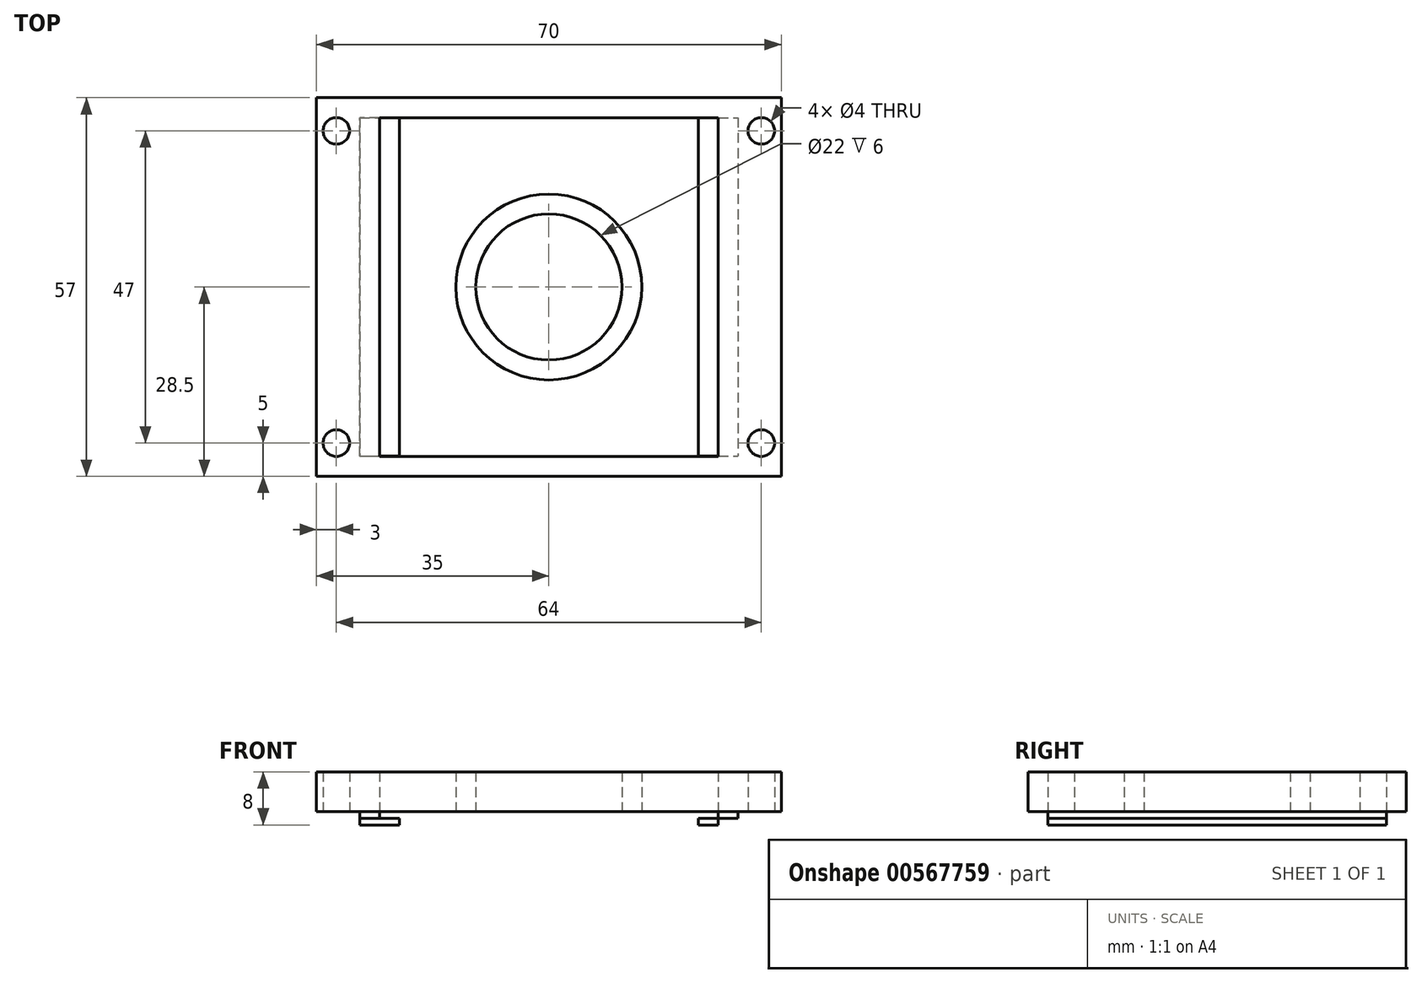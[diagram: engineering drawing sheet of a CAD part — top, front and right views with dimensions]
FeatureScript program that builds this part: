
annotation { "Feature Type Name" : "Feature", "Feature Type Description" : "" }
export const myFeature = defineFeature(function(context is Context, id is Id, definition is map)
    precondition{}
    {
        {
            var Q0;
            Q0=qCreatedBy(makeId("Top.planeOp"),FACE);
            var sketch = newSketch(context, id + "F0", { "sketchPlane" : qUnion([Q0])});
            skCircle(sketch, "E0", {"center": v(0, 0) * mm, "radius": 11 * mm});
            skCircle(sketch, "E1", {"center": v(0, 0) * mm, "radius": 14 * mm});
            skSolve(sketch);
        }
        {
            var Q0;
            Q0=makeQuery(id+"F0.imprint","IMPRINT",FACE,{"disambiguationData":[TD([[makeQuery(id+"F0.imprint","IMPRINT",EDGE,{"derivedFrom":sQuery(id+"F0.wireOp",EDGE,"E0")}),-1.0]])]});
            extrude(context, id + "F1", {"entities" : qUnion([Q0]), "depth" : 6 * mm, "offsetDistance" : 25 * mm});
        }
        {
            var Q0;
            Q0=makeQuery(id+"F1.opExtrude","CAP_FACE",FACE,{"disambiguationData":[OSD([sQuery(id+"F0.wireOp",EDGE,"E0"),sQuery(id+"F0.wireOp",EDGE,"E1")])],"isStart":true});
            var sketch = newSketch(context, id + "F2", { "sketchPlane" : qUnion([Q0])});
            skLineSegment(sketch, "E2.bottom", {"start": v(25.5, -25.5) * mm, "end": v(-25.5, -25.5) * mm});
            skLineSegment(sketch, "E2.top", {"start": v(25.5, 25.5) * mm, "end": v(-25.5, 25.5) * mm});
            skLineSegment(sketch, "E2.left", {"start": v(25.5, -25.5) * mm, "end": v(25.5, 25.5) * mm});
            skLineSegment(sketch, "E2.right", {"start": v(-25.5, -25.5) * mm, "end": v(-25.5, 25.5) * mm});
            skPoint(sketch, "E2.middle", {"position": v(0, 0) * mm});
            skLineSegment(sketch, "E3.bottom", {"start": v(28.5, 28.5) * mm, "end": v(-28.5, 28.5) * mm});
            skLineSegment(sketch, "E3.top", {"start": v(28.5, -28.5) * mm, "end": v(-28.5, -28.5) * mm});
            skLineSegment(sketch, "E3.left", {"start": v(28.5, 28.5) * mm, "end": v(28.5, -28.5) * mm});
            skLineSegment(sketch, "E3.right", {"start": v(-28.5, 28.5) * mm, "end": v(-28.5, -28.5) * mm});
            skLineSegment(sketch, "E4.bottom", {"start": v(-25.5, -2.53) * mm, "end": v(-13.7, -2.53) * mm});
            skLineSegment(sketch, "E4.top", {"start": v(-25.5, 2.53) * mm, "end": v(-13.7, 2.53) * mm});
            skLineSegment(sketch, "E4.left", {"start": v(-25.5, -2.53) * mm, "end": v(-25.5, 2.53) * mm});
            skLineSegment(sketch, "E4.right", {"start": v(25.5, -2.53) * mm, "end": v(25.5, 2.53) * mm});
            skLineSegment(sketch, "E5.bottom", {"start": v(-2.33, 25.5) * mm, "end": v(2.33, 25.5) * mm});
            skLineSegment(sketch, "E5.top", {"start": v(-2.33, -25.5) * mm, "end": v(2.33, -25.5) * mm});
            skLineSegment(sketch, "E5.left", {"start": v(-2.33, 25.5) * mm, "end": v(-2.33, 13.74) * mm});
            skLineSegment(sketch, "E5.right", {"start": v(2.33, 25.5) * mm, "end": v(2.33, 13.74) * mm});
            skArc(sketch, "E6", {"start": v(2.33, 13.74) * mm, "mid": v(0, 13.94) * mm, "end": v(-2.33, 13.74) * mm});
            skLineSegment(sketch, "E7.trimOffspring", {"start": v(13.7, -2.53) * mm, "end": v(25.5, -2.53) * mm});
            skLineSegment(sketch, "E8.trimOffspring", {"start": v(13.7, 2.53) * mm, "end": v(25.5, 2.53) * mm});
            skLineSegment(sketch, "E9.trimOffspring", {"start": v(2.33, -13.74) * mm, "end": v(2.33, -25.5) * mm});
            skLineSegment(sketch, "E10.trimOffspring", {"start": v(-2.33, -13.74) * mm, "end": v(-2.33, -25.5) * mm});
            skArc(sketch, "E11.trimOffspring", {"start": v(-2.33, -13.74) * mm, "mid": v(0, -13.94) * mm, "end": v(2.33, -13.74) * mm});
            skArc(sketch, "E12.trimOffspring", {"start": v(13.7, -2.53) * mm, "mid": v(13.94, 0) * mm, "end": v(13.7, 2.53) * mm});
            skArc(sketch, "E13.trimOffspring", {"start": v(-13.7, 2.53) * mm, "mid": v(-13.94, 0) * mm, "end": v(-13.7, -2.53) * mm});
            skSolve(sketch);
        }
        {
            var Q0;
            Q0 = qSketchRegion(id + "F2", true);
            var Q1;
            {var subQ0=sQuery(id+"F2.wireOp",EDGE,"E5.bottom");Q1=makeQuery(id+"F2.imprint","IMPRINT",FACE,{"disambiguationData":[TD([[makeQuery(id+"F2.imprint","IMPRINT",EDGE,{"derivedFrom":subQ0}),-1.0]])]});}
            var Q2;
            {var subQ0=sQuery(id+"F2.wireOp",EDGE,"E4.left");Q2=makeQuery(id+"F2.imprint","IMPRINT",FACE,{"disambiguationData":[TD([[makeQuery(id+"F2.imprint","IMPRINT",EDGE,{"derivedFrom":subQ0}),-1.0]])]});}
            var Q3;
            {var subQ0=sQuery(id+"F2.wireOp",EDGE,"E5.top");Q3=makeQuery(id+"F2.imprint","IMPRINT",FACE,{"disambiguationData":[TD([[makeQuery(id+"F2.imprint","IMPRINT",EDGE,{"derivedFrom":subQ0}),1.0]])]});}
            var Q4;
            {var subQ0=sQuery(id+"F2.wireOp",EDGE,"E4.right");Q4=makeQuery(id+"F2.imprint","IMPRINT",FACE,{"disambiguationData":[TD([[makeQuery(id+"F2.imprint","IMPRINT",EDGE,{"derivedFrom":subQ0}),1.0]])]});}
            extrude(context, id + "F3", {"entities" : qUnion([Q0, Q1, Q2, Q3, Q4]), "oppositeDirection" : true, "depth" : 6 * mm, "offsetDistance" : 25 * mm});
        }
        {
            var Q0;
            Q0=makeQuery(id+"F1.opExtrude","SWEPT_BODY",BODY,{"disambiguationData":[OSD([sQuery(id+"F0.wireOp",EDGE,"E0"),sQuery(id+"F0.wireOp",EDGE,"E1")])]});
            var Q1;
            Q1=makeQuery(id+"F3.opExtrude","SWEPT_BODY",BODY,{"disambiguationData":[OSD([sQuery(id+"F0.wireOp",EDGE,"E1"),sQuery(id+"F2.wireOp",EDGE,"E2.bottom"),sQuery(id+"F2.wireOp",EDGE,"E2.top"),sQuery(id+"F2.wireOp",EDGE,"E2.left"),sQuery(id+"F2.wireOp",EDGE,"E2.right"),sQuery(id+"F2.wireOp",EDGE,"E3.bottom"),sQuery(id+"F2.wireOp",EDGE,"E3.top"),sQuery(id+"F2.wireOp",EDGE,"E3.left"),sQuery(id+"F2.wireOp",EDGE,"E3.right"),sQuery(id+"F2.wireOp",EDGE,"E4.bottom"),sQuery(id+"F2.wireOp",EDGE,"E4.top"),sQuery(id+"F2.wireOp",EDGE,"E5.left"),sQuery(id+"F2.wireOp",EDGE,"E5.right"),sQuery(id+"F2.wireOp",EDGE,"E7.trimOffspring"),sQuery(id+"F2.wireOp",EDGE,"E8.trimOffspring"),sQuery(id+"F2.wireOp",EDGE,"E9.trimOffspring"),sQuery(id+"F2.wireOp",EDGE,"E10.trimOffspring")])]});
            booleanBodies(context, id + "F4", {"operationType" : BooleanOperationType.UNION, "tools" : qUnion([Q0, Q1])});
        }
        {
            var Q0;
            {var subQ0=sQuery(id+"F0.wireOp",EDGE,"E1");Q0=makeQuery(id+"F4.opBoolean","MERGE",FACE,{"derivedFrom":[makeQuery(id+"F1.opExtrude","CAP_FACE",FACE,{"disambiguationData":[OSD([sQuery(id+"F0.wireOp",EDGE,"E0"),subQ0])],"isStart":true}),makeQuery(id+"F3.opExtrude","CAP_FACE",FACE,{"disambiguationData":[OSD([subQ0,sQuery(id+"F2.wireOp",EDGE,"E2.bottom"),sQuery(id+"F2.wireOp",EDGE,"E2.top"),sQuery(id+"F2.wireOp",EDGE,"E2.left"),sQuery(id+"F2.wireOp",EDGE,"E2.right"),sQuery(id+"F2.wireOp",EDGE,"E3.bottom"),sQuery(id+"F2.wireOp",EDGE,"E3.top"),sQuery(id+"F2.wireOp",EDGE,"E3.left"),sQuery(id+"F2.wireOp",EDGE,"E3.right"),sQuery(id+"F2.wireOp",EDGE,"E4.bottom"),sQuery(id+"F2.wireOp",EDGE,"E4.top"),sQuery(id+"F2.wireOp",EDGE,"E5.left"),sQuery(id+"F2.wireOp",EDGE,"E5.right"),sQuery(id+"F2.wireOp",EDGE,"E7.trimOffspring"),sQuery(id+"F2.wireOp",EDGE,"E8.trimOffspring"),sQuery(id+"F2.wireOp",EDGE,"E9.trimOffspring"),sQuery(id+"F2.wireOp",EDGE,"E10.trimOffspring")])],"isStart":true})]});}
            var sketch = newSketch(context, id + "F5", { "sketchPlane" : qUnion([Q0])});
            skLineSegment(sketch, "E14.bottom", {"start": v(25.5, -25.5) * mm, "end": v(28.5, -25.5) * mm});
            skLineSegment(sketch, "E14.top", {"start": v(25.5, 25.48) * mm, "end": v(28.5, 25.48) * mm});
            skLineSegment(sketch, "E14.left", {"start": v(25.5, -25.5) * mm, "end": v(25.5, 25.48) * mm});
            skLineSegment(sketch, "E14.right", {"start": v(28.5, -25.5) * mm, "end": v(28.5, 25.48) * mm});
            skLineSegment(sketch, "E15.bottom", {"start": v(-25.5, -25.5) * mm, "end": v(-28.5, -25.5) * mm});
            skLineSegment(sketch, "E15.top", {"start": v(-25.5, 25.5) * mm, "end": v(-28.5, 25.5) * mm});
            skLineSegment(sketch, "E15.left", {"start": v(-25.5, -25.5) * mm, "end": v(-25.5, 25.5) * mm});
            skLineSegment(sketch, "E15.right", {"start": v(-28.5, -25.5) * mm, "end": v(-28.5, 25.5) * mm});
            skSolve(sketch);
        }
        {
            var Q0;
            Q0 = qSketchRegion(id + "F5", true);
            extrude(context, id + "F6", {"entities" : qUnion([Q0]), "operationType" : NewBodyOperationType.ADD, "depth" : 1 * mm, "offsetDistance" : 25 * mm});
        }
        {
            var Q0;
            Q0=makeQuery(id+"F6.opExtrude","CAP_FACE",FACE,{"disambiguationData":[OSD([sQuery(id+"F5.wireOp",EDGE,"E14.bottom"),sQuery(id+"F5.wireOp",EDGE,"E14.top"),sQuery(id+"F5.wireOp",EDGE,"E14.left"),sQuery(id+"F5.wireOp",EDGE,"E14.right")])],"isStart":false});
            var sketch = newSketch(context, id + "F7", { "sketchPlane" : qUnion([Q0])});
            skLineSegment(sketch, "E16.bottom", {"start": v(28.5, -25.5) * mm, "end": v(22.5, -25.5) * mm});
            skLineSegment(sketch, "E16.top", {"start": v(28.5, 25.48) * mm, "end": v(22.5, 25.48) * mm});
            skLineSegment(sketch, "E16.left", {"start": v(28.5, -25.5) * mm, "end": v(28.5, 25.48) * mm});
            skLineSegment(sketch, "E16.right", {"start": v(22.5, -25.5) * mm, "end": v(22.5, 25.48) * mm});
            skLineSegment(sketch, "E17.bottom", {"start": v(-28.5, 25.48) * mm, "end": v(-22.5, 25.48) * mm});
            skLineSegment(sketch, "E17.top", {"start": v(-28.5, -25.49) * mm, "end": v(-22.5, -25.49) * mm});
            skLineSegment(sketch, "E17.left", {"start": v(-28.5, 25.48) * mm, "end": v(-28.5, -25.49) * mm});
            skLineSegment(sketch, "E17.right", {"start": v(-22.5, 25.48) * mm, "end": v(-22.5, -25.49) * mm});
            skSolve(sketch);
        }
        {
            var Q0;
            Q0=makeQuery(id+"F7.imprint","IMPRINT",FACE,{"disambiguationData":[TD([[makeQuery(id+"F7.imprint","IMPRINT",EDGE,{"derivedFrom":sQuery(id+"F7.wireOp",EDGE,"E17.bottom")}),-1.0]])]});
            var Q1;
            {var subQ2=sQuery(id+"F7.wireOp",EDGE,"E16.right");Q1=makeQuery(id+"F7.imprint","IMPRINT",FACE,{"disambiguationData":[TD([[makeQuery(id+"F7.imprint","IMPRINT",EDGE,{"derivedFrom":subQ2}),-1.0]])]});}
            var Q2;
            {var subQ2=sQuery(id+"F7.wireOp",EDGE,"E16.left");Q2=makeQuery(id+"F7.imprint","IMPRINT",FACE,{"disambiguationData":[TD([[makeQuery(id+"F7.imprint","IMPRINT",EDGE,{"derivedFrom":subQ2}),-1.0]])]});}
            extrude(context, id + "F8", {"entities" : qUnion([Q0, Q1, Q2]), "operationType" : NewBodyOperationType.ADD, "depth" : 1 * mm, "offsetDistance" : 25 * mm});
        }
        {
            var Q0;
            Q0=qCreatedBy(makeId("Top.planeOp"),FACE);
            var sketch = newSketch(context, id + "F9", { "sketchPlane" : qUnion([Q0])});
            skLineSegment(sketch, "E18.bottom", {"start": v(-35, 28.5) * mm, "end": v(35, 28.5) * mm});
            skLineSegment(sketch, "E18.top", {"start": v(-35, -28.5) * mm, "end": v(35, -28.5) * mm});
            skLineSegment(sketch, "E18.left", {"start": v(-35, 28.5) * mm, "end": v(-35, -28.5) * mm});
            skLineSegment(sketch, "E18.right", {"start": v(35, 28.5) * mm, "end": v(35, -28.5) * mm});
            skPoint(sketch, "E18.middle", {"position": v(0, 0) * mm});
            skLineSegment(sketch, "E19.bottom", {"start": v(-28.5, 28.5) * mm, "end": v(28.5, 28.5) * mm});
            skLineSegment(sketch, "E19.top", {"start": v(-28.5, -28.5) * mm, "end": v(28.5, -28.5) * mm});
            skLineSegment(sketch, "E19.left", {"start": v(-28.5, 28.5) * mm, "end": v(-28.5, -28.5) * mm});
            skLineSegment(sketch, "E19.right", {"start": v(28.5, 28.5) * mm, "end": v(28.5, -28.5) * mm});
            skCircle(sketch, "E20", {"center": v(-32, -23.5) * mm, "radius": 2 * mm});
            skCircle(sketch, "E21", {"center": v(-32, 23.5) * mm, "radius": 2 * mm});
            skCircle(sketch, "E22", {"center": v(32, -23.5) * mm, "radius": 2 * mm});
            skCircle(sketch, "E23", {"center": v(32, 23.5) * mm, "radius": 2 * mm});
            skSolve(sketch);
        }
        {
            var Q0;
            {var subQ1=sQuery(id+"F9.wireOp",EDGE,"E18.left");Q0=makeQuery(id+"F9.imprint","IMPRINT",FACE,{"disambiguationData":[TD([[makeQuery(id+"F9.imprint","IMPRINT",EDGE,{"derivedFrom":subQ1}),1.0]])]});}
            var Q1;
            {var subQ1=sQuery(id+"F9.wireOp",EDGE,"E18.right");Q1=makeQuery(id+"F9.imprint","IMPRINT",FACE,{"disambiguationData":[TD([[makeQuery(id+"F9.imprint","IMPRINT",EDGE,{"derivedFrom":subQ1}),-1.0]])]});}
            extrude(context, id + "F10", {"entities" : qUnion([Q0, Q1]), "operationType" : NewBodyOperationType.ADD, "depth" : 6 * mm, "offsetDistance" : 25 * mm});
        }
    });
